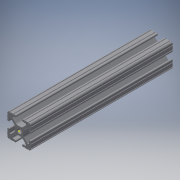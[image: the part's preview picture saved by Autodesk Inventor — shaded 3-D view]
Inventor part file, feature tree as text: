
AUTODESK INVENTOR PART (.ipt)
format: ipt  version: 2018 (Build 220112000, 112)  size: 226,816 bytes
history: native  units: in
note: dims shown in document units (in); Inventor stores cm internally (conversion verified against a paired STEP export)
features: sketch x2, extrude x1
ambient origin geometry x8: Origin, YZ Plane, XZ Plane, XY Plane, X Axis, Y Axis, Z Axis, Center Point
bodies: Solid1 (feature_tree)
feature tree (3):
  extrude  "Extrusion1"  [1 undecoded]
  sketch  "Sketch2"
  sketch  "Sketch1"  dims[d0=6.0in d1=0.0in]
note: 1 required parameter value undecoded (feature->parameter linkage not recoverable at this tier; creation-order binding heuristic only, values carry confidence <= 0.55)
